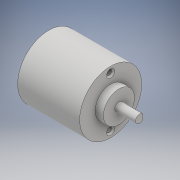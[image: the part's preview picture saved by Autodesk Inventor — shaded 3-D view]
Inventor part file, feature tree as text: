
AUTODESK INVENTOR PART (.ipt)
format: ipt  version: 2018 (Build 220112000, 112)  size: 146,432 bytes
history: native  units: mm
features: sketch x6, extrude x5, hole x1, fillet x1
ambient origin geometry x8: Origin, YZ Plane, XZ Plane, XY Plane, X Axis, Y Axis, Z Axis, Center Point
bodies: Solid1 (feature_tree)
feature tree (13):
  extrude  "Extrusion1"  Depth=30.0mm TaperAngle=0.0deg
  extrude  "Extrusion2"  Depth=4.0mm TaperAngle=0.0deg
  extrude  "Extrusion3"  Depth=10.0mm TaperAngle=0.0deg
  extrude  "Extrusion4"  Depth=8.0mm TaperAngle=0.0deg
  hole  "Hole1"  [1 undecoded]
  extrude  "Extrusion5"  Depth=8.0mm
  fillet  "Fillet1"  Radius=4.0mm
  sketch  "Sketch1"  dims[d0=30.0mm d1=30.0mm d2=0.0mm]
  sketch  "Sketch2"  dims[d3=15.0mm d4=4.0mm d5=0.0mm]
  sketch  "Sketch3"  dims[d6=4.0mm d7=10.0mm d8=0.0mm]
  sketch  "Sketch4"  dims[d9=3.5mm d10=8.0mm d11=0.0mm]
  sketch  "Sketch5"  dims[d12=24.0mm]
  sketch  "Sketch6"  dims[d13=2.459mm d14=6.0mm d15=4.0mm d16=2.0mm d17=90.0deg d18=8.8mm d19=20.594885mm d20=9.0mm d21=8.0mm d22=4.0mm d23=0.0mm d24=1.5mm]
note: 1 required parameter value undecoded (feature->parameter linkage not recoverable at this tier; creation-order binding heuristic only, values carry confidence <= 0.55)
